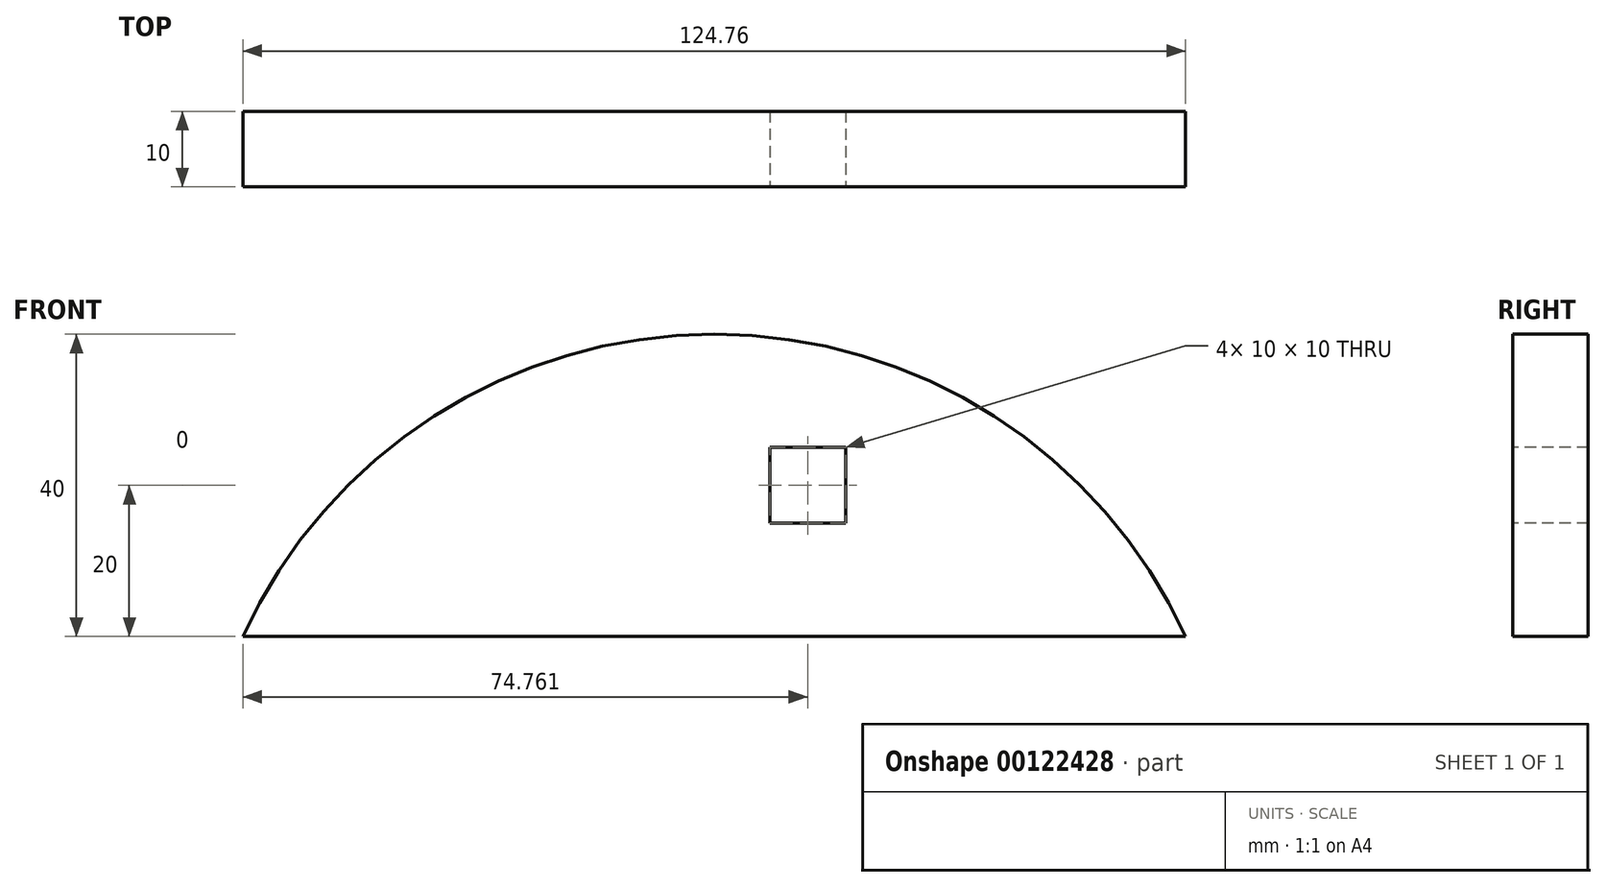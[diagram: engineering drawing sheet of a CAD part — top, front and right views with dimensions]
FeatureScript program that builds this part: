
annotation { "Feature Type Name" : "Feature", "Feature Type Description" : "" }
export const myFeature = defineFeature(function(context is Context, id is Id, definition is map)
    precondition{}
    {
        {
            var Q0;
            Q0=qCreatedBy(makeId("Front.planeOp"),FACE);
            var sketch = newSketch(context, id + "F0", { "sketchPlane" : qUnion([Q0])});
            skArc(sketch, "E0", {"start": v(62.38, 28.64) * mm, "mid": v(0, 68.64) * mm, "end": v(-62.38, 28.64) * mm});
            skLineSegment(sketch, "E1", {"start": v(-62.38, 28.64) * mm, "end": v(62.38, 28.64) * mm});
            skSolve(sketch);
        }
        {
            var Q0;
            Q0 = qSketchRegion(id + "F0", true);
            extrude(context, id + "F1", {"entities" : qUnion([Q0]), "depth" : 10 * mm});
        }
        {
            var Q0;
            Q0=makeQuery(id+"F1.opExtrude","CAP_FACE",FACE,{"disambiguationData":[OSD([sQuery(id+"F0.wireOp",EDGE,"E0"),sQuery(id+"F0.wireOp",EDGE,"E1")])],"isStart":false});
            var sketch = newSketch(context, id + "F2", { "sketchPlane" : qUnion([Q0])});
            skLineSegment(sketch, "E2.bottom", {"start": v(7.38, 53.64) * mm, "end": v(17.38, 53.64) * mm});
            skLineSegment(sketch, "E2.top", {"start": v(7.38, 43.64) * mm, "end": v(17.38, 43.64) * mm});
            skLineSegment(sketch, "E2.left", {"start": v(7.38, 53.64) * mm, "end": v(7.38, 43.64) * mm});
            skLineSegment(sketch, "E2.right", {"start": v(17.38, 53.64) * mm, "end": v(17.38, 43.64) * mm});
            skSolve(sketch);
        }
        {
            var Q0;
            Q0 = qSketchRegion(id + "F2", true);
            extrude(context, id + "F3", {"entities" : qUnion([Q0]), "operationType" : NewBodyOperationType.REMOVE, "endBound" : BoundingType.THROUGH_ALL, "oppositeDirection" : true, "depth" : 25 * mm});
        }
    });
